# Revit family: RAUPIANO PLUS Double Socket
name_source: partatom
category: Pipe Fittings
revit_build: Autodesk Revit MEP 2012 (Build: 20110309_2315(x64)
units: mm (PartAtom-declared; Revit-internal decimal feet)

## types (1)
- Standard
    A1 = 123144-001
    A2 = 121484-001
    A3 = 121584-001
    A4 = 123344-001
    A5 = 121494-001
    A6 = 120474-001
    A7 = 124047-001
    A8 = 123784-001
    Description = REHAU RAUPIANO PLUS double socket
    Fail = No article found
    K Coefficient Table = Reducer/Coupling/Union/Increaser
    Loss Method = K Coefficient from Table
    M1 = 11231441001
    M2 = 11214841001
    M3 = 11215841001
    M4 = 11233441001
    M5 = 11214941001
    M6 = 11204741001
    M7 = 11240471001
    M8 = 11237841001
    Manufacturer = REHAU
    T1 = DN 40
    T2 = DN 50
    T3 = DN 75
    T4 = DN 90
    T5 = DN 110
    T6 = DN 125
    T7 = DN 160
    T8 = DN 200
    Type Comments = RAU-PP; Push-fit; White

## geometry (parser evidence)
native form markers: Sweep x1
no freeform markers — native parametric forms only
